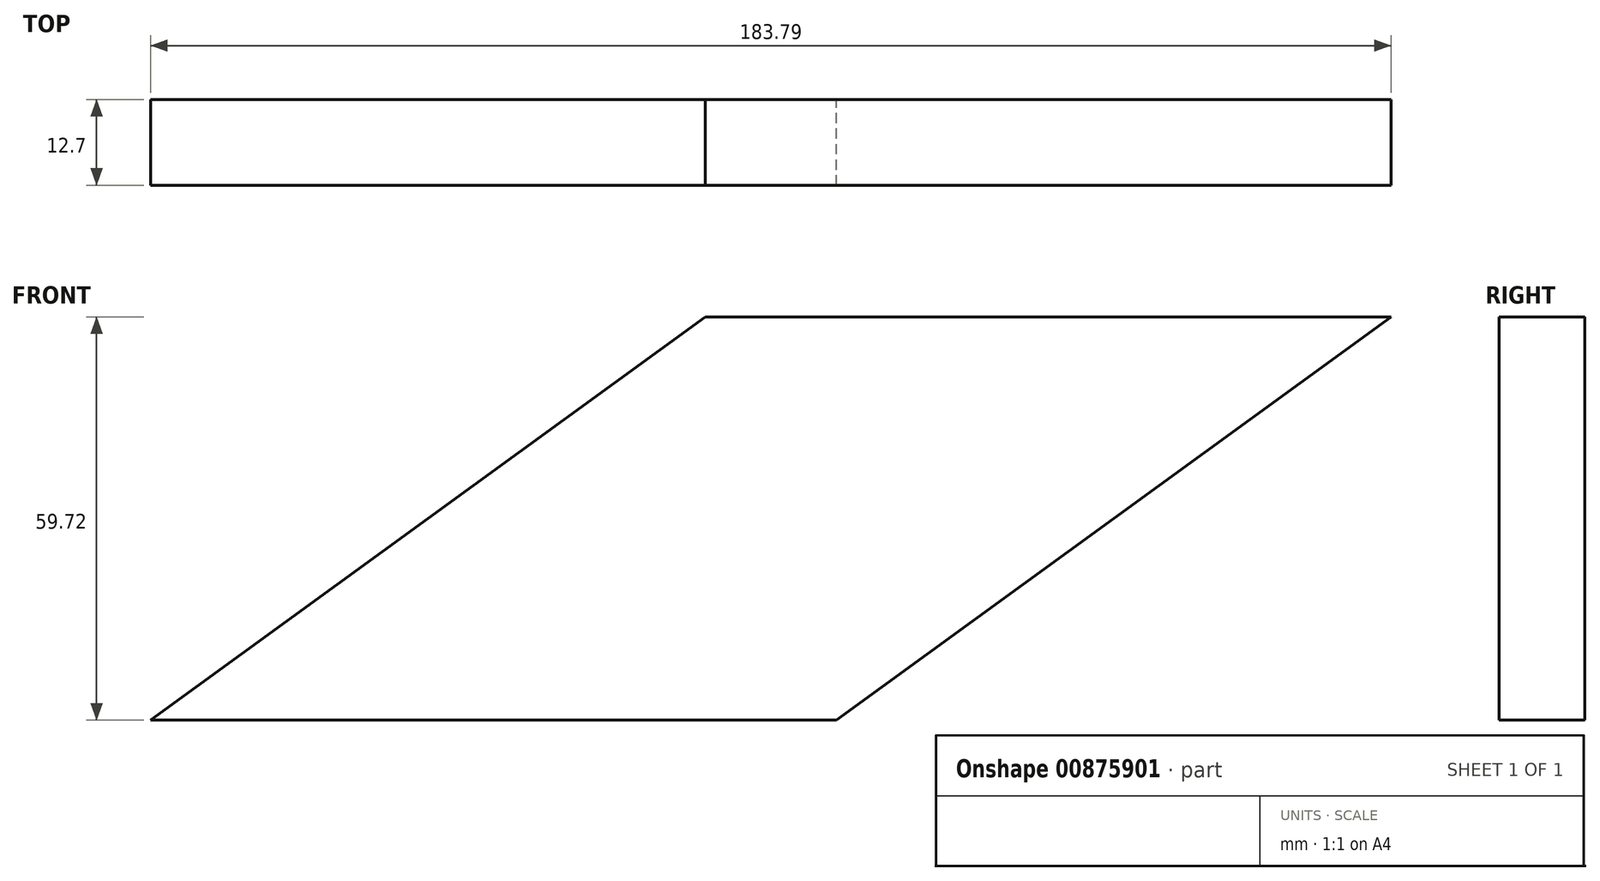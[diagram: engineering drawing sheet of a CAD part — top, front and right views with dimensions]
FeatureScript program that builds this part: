
annotation { "Feature Type Name" : "Feature", "Feature Type Description" : "" }
export const myFeature = defineFeature(function(context is Context, id is Id, definition is map)
    precondition{}
    {
        {
            var Q0;
            Q0=qCreatedBy(makeId("Front.planeOp"),FACE);
            var sketch = newSketch(context, id + "F0", { "sketchPlane" : qUnion([Q0])});
            skLineSegment(sketch, "E0", {"start": v(-172.78, -45.21) * mm, "end": v(-71.18, -45.21) * mm});
            skLineSegment(sketch, "E1", {"start": v(-71.18, -45.21) * mm, "end": v(-153.37, -104.93) * mm});
            skLineSegment(sketch, "E2", {"start": v(-153.37, -104.93) * mm, "end": v(-254.97, -104.93) * mm});
            skLineSegment(sketch, "E3", {"start": v(-254.97, -104.93) * mm, "end": v(-172.78, -45.21) * mm});
            skSolve(sketch);
        }
        {
            var Q0;
            Q0=makeQuery(id+"F0.imprint","IMPRINT",FACE,{"disambiguationData":[TD([[makeQuery(id+"F0.imprint","IMPRINT",EDGE,{"derivedFrom":sQuery(id+"F0.wireOp",EDGE,"E0")}),-1.0]])]});
            extrude(context, id + "F1", {"entities" : qUnion([Q0]), "depth" : 12.7 * mm, "offsetDistance" : 25.4 * mm});
        }
    });
